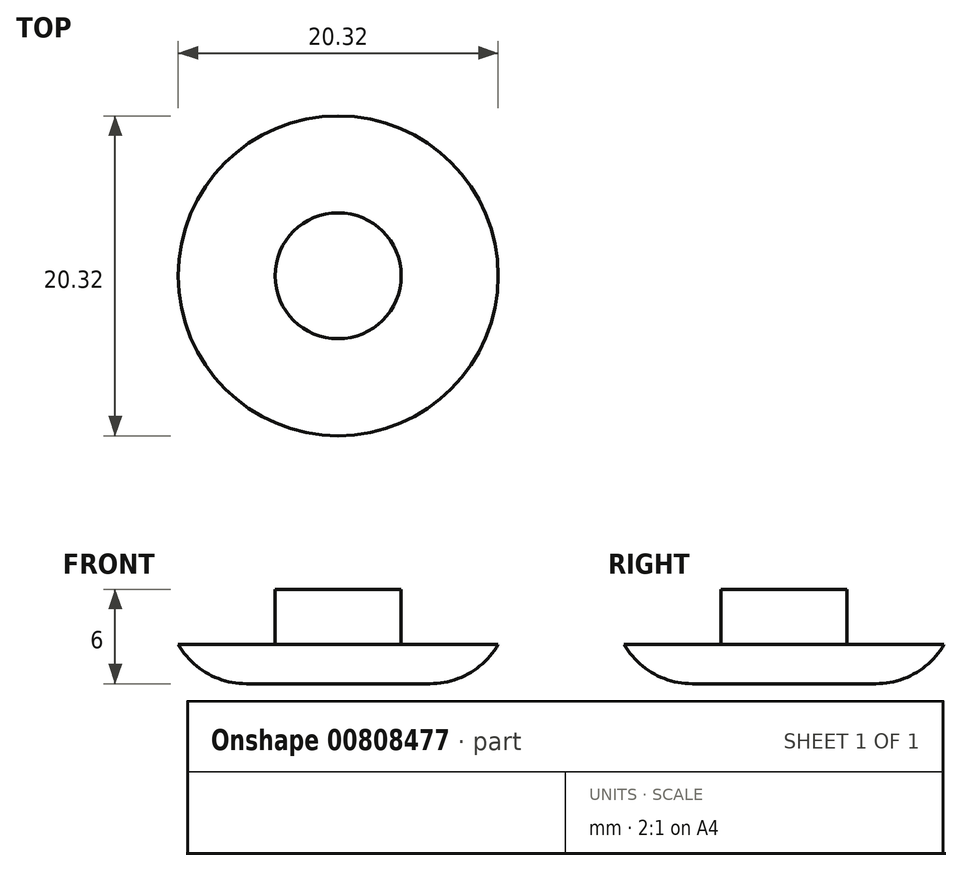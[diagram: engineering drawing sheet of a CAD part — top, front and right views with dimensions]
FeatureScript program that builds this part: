
annotation { "Feature Type Name" : "Feature", "Feature Type Description" : "" }
export const myFeature = defineFeature(function(context is Context, id is Id, definition is map)
    precondition{}
    {
        {
            var Q0;
            Q0=qCreatedBy(makeId("Top.planeOp"),FACE);
            var sketch = newSketch(context, id + "F0", { "sketchPlane" : qUnion([Q0])});
            skCircle(sketch, "E0", {"center": v(0, 0) * mm, "radius": 10.16 * mm});
            skSolve(sketch);
        }
        {
            var Q0;
            Q0 = qSketchRegion(id + "F0", true);
            extrude(context, id + "F1", {"entities" : qUnion([Q0]), "depth" : 2.5 * mm, "offsetDistance" : 25 * mm});
        }
        {
            var Q0;
            Q0=makeQuery(id+"F1.opExtrude","CAP_FACE",FACE,{"disambiguationData":[OSD([sQuery(id+"F0.wireOp",EDGE,"E0")])],"isStart":false});
            var sketch = newSketch(context, id + "F2", { "sketchPlane" : qUnion([Q0])});
            skCircle(sketch, "E1", {"center": v(0, 0) * mm, "radius": 4 * mm});
            skSolve(sketch);
        }
        {
            var Q0;
            Q0 = qSketchRegion(id + "F2", true);
            extrude(context, id + "F3", {"entities" : qUnion([Q0]), "operationType" : NewBodyOperationType.ADD, "depth" : 7 * mm / 2, "offsetDistance" : 25 * mm});
        }
        {
            var Q0;
            Q0=makeQuery(id+"F1.opExtrude","CAP_EDGE",EDGE,{"disambiguationData":[OSD([sQuery(id+"F0.wireOp",EDGE,"E0")])],"isStart":true});
            fillet(context, id + "F4", {"entities" : qUnion([Q0]), "radius" : 5 * mm, "tangentPropagation" : true, "allowEdgeOverflow" : false});
        }
    });
